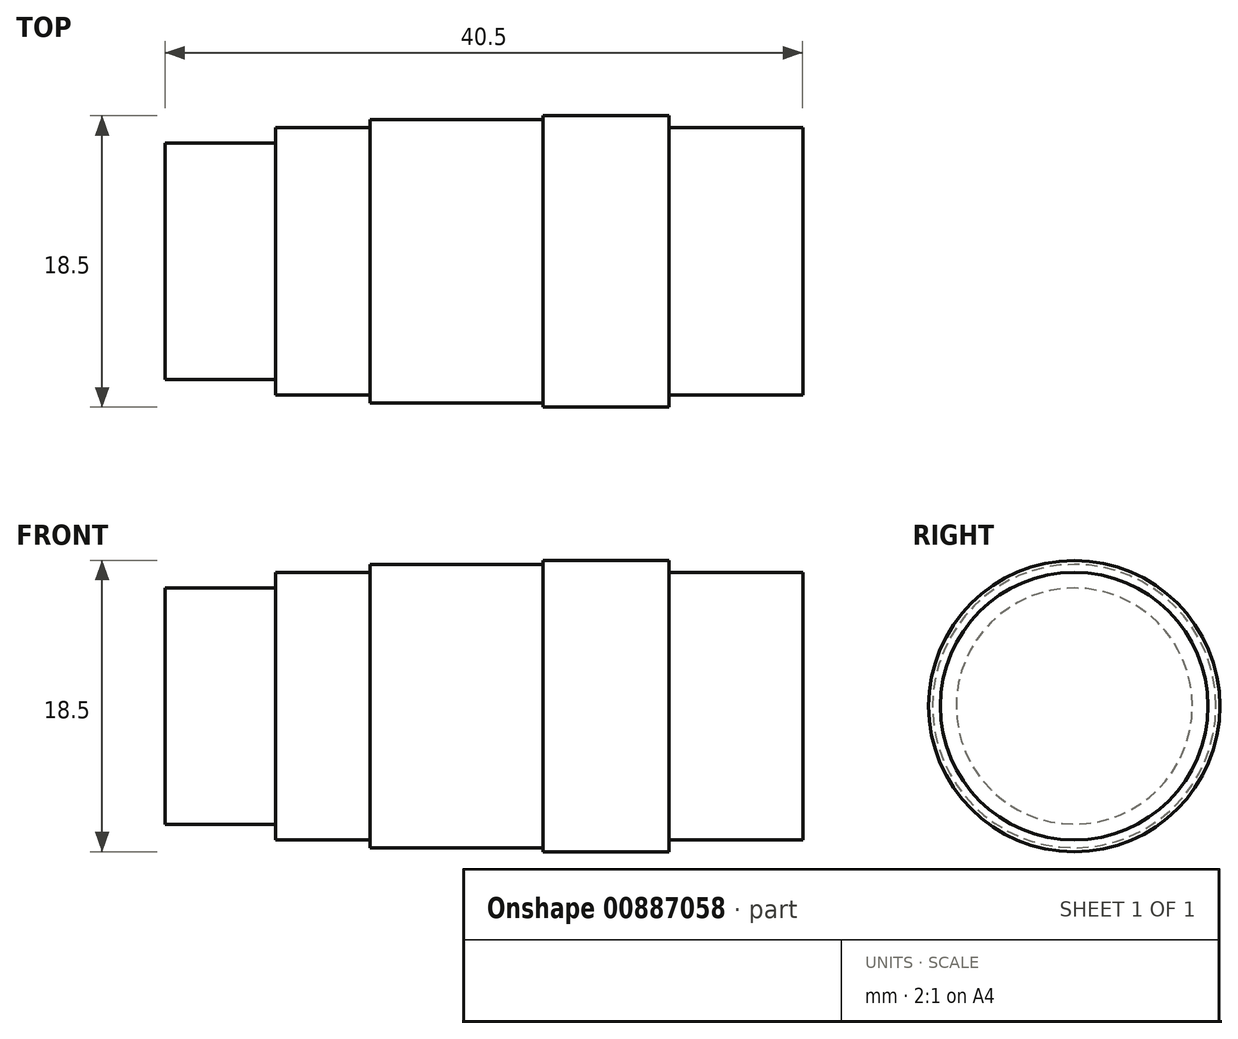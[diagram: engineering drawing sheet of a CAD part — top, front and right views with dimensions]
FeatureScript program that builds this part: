
annotation { "Feature Type Name" : "Feature", "Feature Type Description" : "" }
export const myFeature = defineFeature(function(context is Context, id is Id, definition is map)
    precondition{}
    {
        {
            var Q0;
            Q0=qCreatedBy(makeId("Front.planeOp"),FACE);
            var sketch = newSketch(context, id + "F0", { "sketchPlane" : qUnion([Q0])});
            skLineSegment(sketch, "E0", {"start": v(-55.55, 0) * mm, "end": v(22.68, 0) * mm});
            skLineSegment(sketch, "E1", {"start": v(22.68, 0) * mm, "end": v(22.68, 8.5) * mm});
            skLineSegment(sketch, "E2", {"start": v(22.68, 8.5) * mm, "end": v(14.18, 8.5) * mm});
            skLineSegment(sketch, "E3", {"start": v(14.18, 8.5) * mm, "end": v(14.18, 9.25) * mm});
            skLineSegment(sketch, "E4", {"start": v(14.18, 9.25) * mm, "end": v(6.18, 9.25) * mm});
            skLineSegment(sketch, "E5", {"start": v(6.18, 9.25) * mm, "end": v(6.18, 9) * mm});
            skLineSegment(sketch, "E6", {"start": v(6.18, 9) * mm, "end": v(-4.82, 9) * mm});
            skLineSegment(sketch, "E7", {"start": v(-4.82, 9) * mm, "end": v(-4.82, 8.5) * mm});
            skLineSegment(sketch, "E8", {"start": v(-4.82, 8.5) * mm, "end": v(-10.82, 8.5) * mm});
            skLineSegment(sketch, "E9", {"start": v(-10.82, 8.5) * mm, "end": v(-10.82, 7.5) * mm});
            skLineSegment(sketch, "E10", {"start": v(-10.82, 7.5) * mm, "end": v(-17.82, 7.5) * mm});
            skLineSegment(sketch, "E11", {"start": v(-17.82, 7.5) * mm, "end": v(-17.82, 0) * mm});
            skSolve(sketch);
        }
        {
            var Q0;
            {var subQ0=sQuery(id+"F0.wireOp",EDGE,"E1");Q0=makeQuery(id+"F0.imprint","IMPRINT",FACE,{"disambiguationData":[TD([[makeQuery(id+"F0.imprint","IMPRINT",EDGE,{"derivedFrom":subQ0}),1.0]])]});}
            var Q1;
            Q1=sQuery(id+"F0.wireOp",EDGE,"E0");
            revolve(context, id + "F1", {"surfaceOperationType" : NewSurfaceOperationType.NEW, "entities" : qUnion([Q0]), "axis" : qUnion([Q1]), "revolveType" : RevolveType.FULL});
        }
    });
